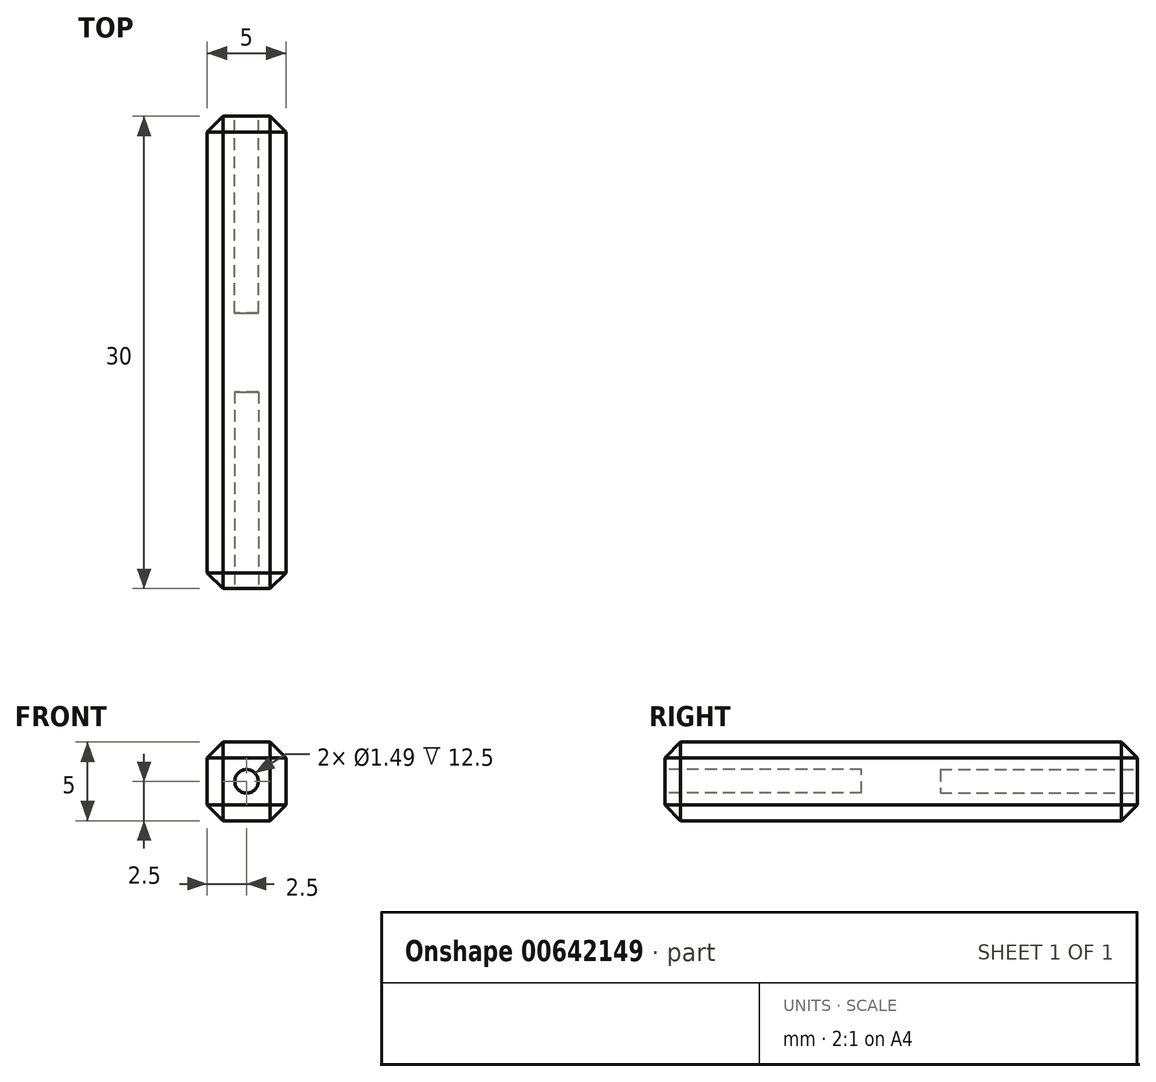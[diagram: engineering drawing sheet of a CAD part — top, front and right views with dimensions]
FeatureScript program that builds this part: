
annotation { "Feature Type Name" : "Feature", "Feature Type Description" : "" }
export const myFeature = defineFeature(function(context is Context, id is Id, definition is map)
    precondition{}
    {
        {
            var Q0;
            Q0=qCreatedBy(makeId("Top.planeOp"),FACE);
            var sketch = newSketch(context, id + "F0", { "sketchPlane" : qUnion([Q0])});
            skLineSegment(sketch, "E0.bottom", {"start": v(-5, 16.88) * mm, "end": v(0, 16.88) * mm});
            skLineSegment(sketch, "E0.top", {"start": v(-5, -13.12) * mm, "end": v(0, -13.12) * mm});
            skLineSegment(sketch, "E0.left", {"start": v(-5, 16.88) * mm, "end": v(-5, -13.12) * mm});
            skLineSegment(sketch, "E0.right", {"start": v(0, 16.88) * mm, "end": v(0, -13.12) * mm});
            skSolve(sketch);
        }
        {
            var Q0;
            Q0=makeQuery(id+"F0.imprint","IMPRINT",FACE,{"disambiguationData":[TD([[makeQuery(id+"F0.imprint","IMPRINT",EDGE,{"derivedFrom":sQuery(id+"F0.wireOp",EDGE,"E0.bottom")}),-1.0]])]});
            extrude(context, id + "F1", {"entities" : qUnion([Q0]), "depth" : 5 * mm, "offsetDistance" : 25.4 * mm});
        }
        {
            var Q0;
            Q0=makeQuery(id+"F1.opExtrude","CAP_EDGE",EDGE,{"disambiguationData":[OSD([sQuery(id+"F0.wireOp",EDGE,"E0.left")])],"isStart":false});
            var Q1;
            Q1=makeQuery(id+"F1.opExtrude","CAP_EDGE",EDGE,{"disambiguationData":[OSD([sQuery(id+"F0.wireOp",EDGE,"E0.right")])],"isStart":false});
            var Q2;
            Q2=makeQuery(id+"F1.opExtrude","CAP_EDGE",EDGE,{"disambiguationData":[OSD([sQuery(id+"F0.wireOp",EDGE,"E0.left")])],"isStart":true});
            var Q3;
            Q3=makeQuery(id+"F1.opExtrude","CAP_EDGE",EDGE,{"disambiguationData":[OSD([sQuery(id+"F0.wireOp",EDGE,"E0.right")])],"isStart":true});
            var Q4;
            Q4=makeQuery(id+"F1.opExtrude","CAP_EDGE",EDGE,{"disambiguationData":[OSD([sQuery(id+"F0.wireOp",EDGE,"E0.bottom")])],"isStart":true});
            var Q5;
            Q5=makeQuery(id+"F1.opExtrude","SWEPT_EDGE",EDGE,{"disambiguationData":[OSD([sQuery(id+"F0.wireOp",EDGE,"E0.bottom"),sQuery(id+"F0.wireOp",EDGE,"E0.left")])]});
            var Q6;
            Q6=makeQuery(id+"F1.opExtrude","CAP_EDGE",EDGE,{"disambiguationData":[OSD([sQuery(id+"F0.wireOp",EDGE,"E0.bottom")])],"isStart":false});
            var Q7;
            Q7=makeQuery(id+"F1.opExtrude","SWEPT_EDGE",EDGE,{"disambiguationData":[OSD([sQuery(id+"F0.wireOp",EDGE,"E0.bottom"),sQuery(id+"F0.wireOp",EDGE,"E0.right")])]});
            var Q8;
            Q8=makeQuery(id+"F1.opExtrude","CAP_EDGE",EDGE,{"disambiguationData":[OSD([sQuery(id+"F0.wireOp",EDGE,"E0.top")])],"isStart":true});
            var Q9;
            Q9=makeQuery(id+"F1.opExtrude","SWEPT_EDGE",EDGE,{"disambiguationData":[OSD([sQuery(id+"F0.wireOp",EDGE,"E0.top"),sQuery(id+"F0.wireOp",EDGE,"E0.right")])]});
            var Q10;
            Q10=makeQuery(id+"F1.opExtrude","CAP_EDGE",EDGE,{"disambiguationData":[OSD([sQuery(id+"F0.wireOp",EDGE,"E0.top")])],"isStart":false});
            var Q11;
            Q11=makeQuery(id+"F1.opExtrude","SWEPT_EDGE",EDGE,{"disambiguationData":[OSD([sQuery(id+"F0.wireOp",EDGE,"E0.top"),sQuery(id+"F0.wireOp",EDGE,"E0.left")])]});
            chamfer(context, id + "F2", {"entities" : qUnion([Q0, Q1, Q2, Q3, Q4, Q5, Q6, Q7, Q8, Q9, Q10, Q11]), "width" : 1 * mm, "tangentPropagation" : true});
        }
        {
            var Q0;
            Q0=makeQuery(id+"F1.opExtrude","SWEPT_FACE",FACE,{"disambiguationData":[OSD([sQuery(id+"F0.wireOp",EDGE,"E0.top")])]});
            var sketch = newSketch(context, id + "F3", { "sketchPlane" : qUnion([Q0])});
            skCircle(sketch, "E1", {"center": v(-2.5, 2.5) * mm, "radius": 0.75 * mm});
            skPoint(sketch, "E1.centerSnap0", {"position": v(-1, 2.5) * mm});
            skPoint(sketch, "E1.centerSnap1", {"position": v(-2.5, 4) * mm});
            skSolve(sketch);
        }
        {
            var Q0;
            Q0=makeQuery(id+"F3.imprint","IMPRINT",FACE,{"disambiguationData":[TD([[makeQuery(id+"F3.imprint","IMPRINT",EDGE,{"derivedFrom":sQuery(id+"F3.wireOp",EDGE,"E1")}),1.0]])]});
            extrude(context, id + "F4", {"entities" : qUnion([Q0]), "operationType" : NewBodyOperationType.REMOVE, "oppositeDirection" : true, "depth" : 12.5 * mm, "offsetDistance" : 25.4 * mm});
        }
        {
            var Q0;
            Q0=makeQuery(id+"F1.opExtrude","SWEPT_FACE",FACE,{"disambiguationData":[OSD([sQuery(id+"F0.wireOp",EDGE,"E0.bottom")])]});
            var sketch = newSketch(context, id + "F5", { "sketchPlane" : qUnion([Q0])});
            skCircle(sketch, "E2", {"center": v(2.5, 2.5) * mm, "radius": 0.75 * mm});
            skPoint(sketch, "E2.centerSnap0", {"position": v(4, 2.5) * mm});
            skPoint(sketch, "E2.centerSnap1", {"position": v(2.5, 1) * mm});
            skSolve(sketch);
        }
        {
            var Q0;
            Q0=makeQuery(id+"F5.imprint","IMPRINT",FACE,{"disambiguationData":[TD([[makeQuery(id+"F5.imprint","IMPRINT",EDGE,{"derivedFrom":sQuery(id+"F5.wireOp",EDGE,"E2")}),1.0]])]});
            extrude(context, id + "F6", {"entities" : qUnion([Q0]), "operationType" : NewBodyOperationType.REMOVE, "oppositeDirection" : true, "depth" : 12.5 * mm, "offsetDistance" : 25.4 * mm});
        }
    });
